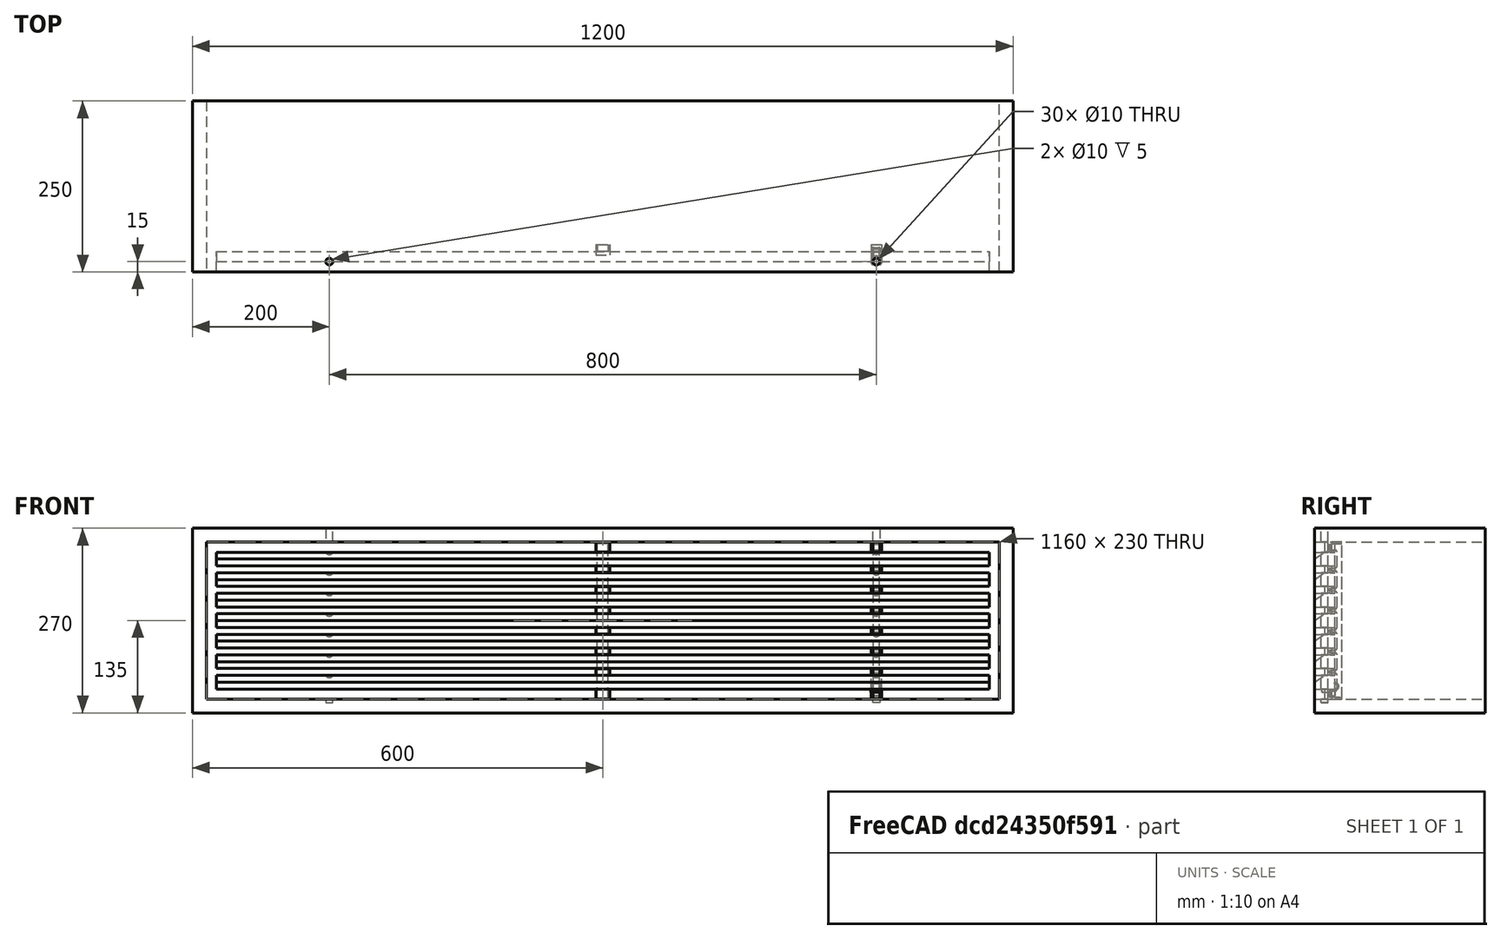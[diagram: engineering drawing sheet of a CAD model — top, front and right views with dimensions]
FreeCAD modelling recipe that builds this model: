
FCSTD DOCUMENT  (FreeCAD 1.0R39109 (Git))
Label: tv cabinet order
License: All rights reserved
objects: TechDraw::DrawViewDimension×24, Sketcher::SketchObject×12, PartDesign::Pad×8, PartDesign::Pocket×7, TechDraw::DrawProjGroupItem×7, PartDesign::Body×6, PartDesign::SubShapeBinder×5, PartDesign::LinearPattern×4, PartDesign::Mirrored×3, PartDesign::Thickness×2, TechDraw::DrawSVGTemplate×2, TechDraw::DrawProjGroup×2, TechDraw::DrawPage×2, TechDraw::DrawViewSection×1, App::DocumentObjectGroup×1, App::VarSet×1
note: 136 computed .brp shape members not serialized (recipe doc carries the construction recipe); baked Part::Feature solids carry a one-line shape summary decoded from their .brp

FEATURE [Sketcher::SketchObject] Sketch
  ArcFitTolerance = 1e-06
  AttachmentSupport = -> [XY_Plane]
  FullyConstrained = true
  MakeInternals = false
  MapMode = 5
  sketch-geometry (5):
    g0: LineSegment StartX=-600 StartY=250 StartZ=0 EndX=-600 EndY=0 EndZ=0
    g1: LineSegment StartX=-600 StartY=0 StartZ=0 EndX=600 EndY=0 EndZ=0
    g2: LineSegment StartX=600 StartY=0 StartZ=0 EndX=600 EndY=250 EndZ=0
    g3: LineSegment StartX=600 StartY=250 StartZ=0 EndX=-600 EndY=250 EndZ=0
    g4: GeomPoint [constr] X=0 Y=125 Z=0
  constraints (13):
    c: Coincident(g0,g1)
    c: Coincident(g1,g2)
    c: Coincident(g2,g3)
    c: Coincident(g3,g0)
    c: Vertical(g0)
    c: Vertical(g2)
    c: Horizontal(g1)
    c: Horizontal(g3)
    c: Symmetric(g2,g0,g4)
    c: PointOnObject(g4,g-2)
    c: DistanceX(g1,g1) = 1200
    c: DistanceY(g2,g2) = 250
    c: PointOnObject(g-1,g1)
FEATURE [PartDesign::Pad] Pad
  Direction = (0,0,1)
  Length = 270
  Length2 = 10
  Profile = -> Sketch
  ReferenceAxis = -> Sketch [N_Axis]
  Suppressed = false
  Type = 0
FEATURE [PartDesign::Thickness] Thickness
  Base = -> Pad [Face2,Face4]
  BaseFeature = -> Pad
  Intersection = false
  Join = 0
  Mode = 0
  Reversed = true
  SupportTransform = false
  Suppressed = false
  Value = 20
FEATURE [Sketcher::SketchObject] Sketch001
  ArcFitTolerance = 1e-06
  AttachmentSupport = -> [XZ_Plane001]
  FullyConstrained = true
  MakeInternals = false
  MapMode = 5
  Placement = pos=(0,0,0) rot=(1,0,0;1.5708rad)
  sketch-geometry (5):
    g0: LineSegment StartX=-565 StartY=55 StartZ=0 EndX=-565 EndY=35 EndZ=0
    g1: LineSegment StartX=-565 StartY=35 StartZ=0 EndX=565 EndY=35 EndZ=0
    g2: LineSegment StartX=565 StartY=35 StartZ=0 EndX=565 EndY=55 EndZ=0
    g3: LineSegment StartX=565 StartY=55 StartZ=0 EndX=-565 EndY=55 EndZ=0
    g4: GeomPoint [constr] X=1e-16 Y=45 Z=0
  constraints (13):
    c: Coincident(g0,g1)
    c: Coincident(g1,g2)
    c: Coincident(g2,g3)
    c: Coincident(g3,g0)
    c: Vertical(g0)
    c: Vertical(g2)
    c: Horizontal(g1)
    c: Horizontal(g3)
    c: Symmetric(g2,g0,g4)
    c: PointOnObject(g4,g-2)
    c: Distance(g2,g2) = 20
    c: Distance(g-1,g1) = 35
    c: DistanceX(g1,g1) = 1130
FEATURE [PartDesign::Pad] Pad001
  Direction = (0,-1,2e-16)
  Length = 30
  Length2 = 10
  Placement = pos=(0,0,0) rot=(1,0,0;1.5708rad)
  Profile = -> Sketch001
  ReferenceAxis = -> Sketch001 [N_Axis]
  Reversed = true
  Suppressed = false
  Type = 0
FEATURE [PartDesign::LinearPattern] LinearPattern
  BaseFeature = -> Pad001
  Direction = -> Z_Axis001
  Length = 180
  Mode = 1
  Occurrences = 7
  Offset = 30
  Placement = pos=(0,0,0) rot=(1,0,0;1.5708rad)
  Suppressed = false
  TransformMode = 1
FEATURE [TechDraw::DrawSVGTemplate] Template
  Height = 210
  Orientation = 1
  Template = /Applications/FreeCAD.app/Contents/Resources/share/Mod/TechDraw/Templates/A4_Landscape_TD.svg
  Width = 297
FEATURE [Sketcher::SketchObject] Sketch002
  ArcFitTolerance = 1e-06
  AttachmentSupport = -> [Thickness]
  FullyConstrained = true
  MakeInternals = false
  MapMode = 5
  Placement = pos=(0,0,270) rot=(0,0,1;0rad)
  sketch-geometry (1):
    g0: Circle CenterX=400 CenterY=15 CenterZ=0 NormalX=0 NormalY=0 NormalZ=1 AngleXU=0 Radius=5
  constraints (3):
    c: Diameter(g0) = 10
    c: DistanceX(g-1,g0) = 400
    c: DistanceY(g-1,g0) = 15
FEATURE [PartDesign::Pocket] Pocket
  BaseFeature = -> Thickness
  Direction = (0,0,-1)
  Length = 0
  Length2 = 5
  Offset = -15
  Profile = -> Sketch002
  ReferenceAxis = -> Sketch002 [N_Axis]
  Suppressed = false
  Type = 3
  UpToFace = -> Thickness [Face2]
FEATURE [PartDesign::Mirrored] Mirrored
  BaseFeature = -> Pocket
  MirrorPlane = -> Sketch002 [V_Axis]
  Originals = -> [Pocket]
  Suppressed = false
  TransformMode = 0
FEATURE [PartDesign::Body] Body
  AllowCompound = true
  Group = -> [Sketch,Pad,Thickness,Sketch002,Pocket,Mirrored]
  Origin = -> Origin
  Tip = -> Mirrored
FEATURE [TechDraw::DrawProjGroupItem] View
  Caption = 前
  CoarseView = false
  Direction = (0,-1,0)
  Focus = 100
  HardHidden = false
  IsoCount = 0
  IsoHidden = false
  IsoVisible = false
  LockPosition = true
  Perspective = false
  Rotation = 0
  RotationVector = (1,0,0)
  Scale = 0.1
  ScaleType = 2
  ScrubCount = 1
  SeamHidden = false
  SeamVisible = false
  SmoothHidden = false
  SmoothVisible = true
  Source = -> [Body]
  Type = 0
  X = 0
  XDirection = (1,0,0)
  Y = 0
FEATURE [TechDraw::DrawProjGroupItem] ProjItem001
  Caption = 下
  CoarseView = false
  Direction = (0,0,-1)
  Focus = 100
  HardHidden = false
  IsoCount = 0
  IsoHidden = false
  IsoVisible = false
  LockPosition = false
  Perspective = false
  Rotation = 0
  RotationVector = (1,0,0)
  Scale = 0.1
  ScaleType = 2
  ScrubCount = 1
  SeamHidden = false
  SeamVisible = false
  SmoothHidden = false
  SmoothVisible = true
  Source = -> [Body]
  Type = 5
  X = 0
  XDirection = (1,0,0)
  Y = -41
FEATURE [TechDraw::DrawProjGroupItem] ProjItem002
  Caption = 右
  CoarseView = false
  Direction = (1,-1e-16,0)
  Focus = 100
  HardHidden = false
  IsoCount = 0
  IsoHidden = false
  IsoVisible = false
  LockPosition = false
  Perspective = false
  Rotation = 0
  RotationVector = (1,0,0)
  Scale = 0.1
  ScaleType = 2
  ScrubCount = 1
  SeamHidden = false
  SeamVisible = false
  SmoothHidden = false
  SmoothVisible = true
  Source = -> [Body]
  Type = 2
  X = 87.5
  XDirection = (1e-16,1,0)
  Y = 0
FEATURE [TechDraw::DrawProjGroupItem] ProjItem
  Caption = 上
  CoarseView = false
  Direction = (0,0,1)
  Focus = 100
  HardHidden = false
  IsoCount = 0
  IsoHidden = false
  IsoVisible = false
  LockPosition = false
  Perspective = false
  Rotation = 0
  RotationVector = (1,0,0)
  Scale = 0.1
  ScaleType = 2
  ScrubCount = 1
  SeamHidden = false
  SeamVisible = false
  SmoothHidden = false
  SmoothVisible = true
  Source = -> [Body]
  Type = 4
  X = 0
  XDirection = (1,0,0)
  Y = 41
FEATURE [TechDraw::DrawProjGroup] ProjGroup
  Anchor = -> View
  AutoDistribute = true
  LockPosition = false
  ProjectionType = 1
  Rotation = 0
  Scale = 0.1
  ScaleType = 2
  Source = -> [Body]
  Views = -> [View,ProjItem001,ProjItem002,ProjItem]
  X = 81.3067
  Y = 133.557
  spacingX = 15
  spacingY = 15
FEATURE [TechDraw::DrawViewDimension] Dimension
  AngleOverride = false
  Arbitrary = false
  ArbitraryTolerances = false
  BoxCorners = (2) [(-60,-13.5,0),(60,13.5,0)]
  EqualTolerance = true
  ExtensionAngle = 0
  FormatSpec = %.2w
  FormatSpecOverTolerance = %+.2w
  FormatSpecUnderTolerance = %+.2w
  Inverted = false
  LineAngle = 0
  LockPosition = false
  MeasureType = 1
  OverTolerance = 0
  References2D = -> [View]
  Rotation = 0
  ScaleType = 0
  TheoreticalExact = false
  Type = 1
  UnderTolerance = 0
  X = 4.02177
  Y = -6.19776
FEATURE [TechDraw::DrawViewDimension] Dimension001
  AngleOverride = false
  Arbitrary = false
  ArbitraryTolerances = false
  BoxCorners = (2) [(-60,-13.5,0),(60,13.5,0)]
  EqualTolerance = true
  ExtensionAngle = 0
  FormatSpec = %.2w
  FormatSpecOverTolerance = %+.2w
  FormatSpecUnderTolerance = %+.2w
  Inverted = false
  LineAngle = 0
  LockPosition = false
  MeasureType = 1
  OverTolerance = 0
  References2D = -> [View]
  Rotation = 0
  ScaleType = 0
  TheoreticalExact = false
  Type = 2
  UnderTolerance = 0
  X = 49.5219
  Y = 0
FEATURE [TechDraw::DrawViewDimension] Dimension002
  AngleOverride = false
  Arbitrary = false
  ArbitraryTolerances = false
  BoxCorners = (2) [(-12.5,-13.5,0),(12.5,13.5,0)]
  EqualTolerance = true
  ExtensionAngle = 0
  FormatSpec = %.2w
  FormatSpecOverTolerance = %+.2w
  FormatSpecUnderTolerance = %+.2w
  Inverted = false
  LineAngle = 0
  LockPosition = false
  MeasureType = 1
  OverTolerance = 0
  References2D = -> [ProjItem002]
  Rotation = 0
  ScaleType = 0
  TheoreticalExact = false
  Type = 1
  UnderTolerance = 0
  X = 0
  Y = -8.38368
FEATURE [TechDraw::DrawViewDimension] Dimension003
  AngleOverride = false
  Arbitrary = false
  ArbitraryTolerances = false
  BoxCorners = (2) [(-60,-12.5,0),(60,12.5,0)]
  EqualTolerance = true
  ExtensionAngle = 0
  FormatSpec = %.2w
  FormatSpecOverTolerance = %+.2w
  FormatSpecUnderTolerance = %+.2w
  Inverted = false
  LineAngle = 0
  LockPosition = false
  MeasureType = 1
  OverTolerance = 0
  References2D = -> [ProjItem]
  Rotation = 0
  ScaleType = 0
  TheoreticalExact = false
  Type = 0
  UnderTolerance = 0
  X = -46.9988
  Y = -6.85586
FEATURE [TechDraw::DrawViewDimension] Dimension004
  AngleOverride = false
  Arbitrary = false
  ArbitraryTolerances = false
  BoxCorners = (2) [(-60,-12.5,0),(60,12.5,0)]
  EqualTolerance = true
  ExtensionAngle = 0
  FormatSpec = %.2w
  FormatSpecOverTolerance = %+.2w
  FormatSpecUnderTolerance = %+.2w
  Inverted = false
  LineAngle = 0
  LockPosition = false
  MeasureType = 1
  OverTolerance = 0
  References2D = -> [ProjItem]
  Rotation = 0
  ScaleType = 0
  TheoreticalExact = false
  Type = 0
  UnderTolerance = 0
  X = -30.5049
  Y = -7.0879
FEATURE [TechDraw::DrawViewDimension] Dimension005
  AngleOverride = false
  Arbitrary = false
  ArbitraryTolerances = false
  BoxCorners = (2) [(-60,-12.5,0),(60,12.5,0)]
  EqualTolerance = true
  ExtensionAngle = 0
  FormatSpec = ⌀%.2w 通孔
  FormatSpecOverTolerance = %+.2w
  FormatSpecUnderTolerance = %+.2w
  Inverted = false
  LineAngle = 0
  LockPosition = false
  MeasureType = 1
  OverTolerance = 0
  References2D = -> [ProjItem]
  Rotation = 0
  ScaleType = 0
  TheoreticalExact = false
  Type = 5
  UnderTolerance = 0
  X = -29.1444
  Y = 3.68719
FEATURE [TechDraw::DrawViewDimension] Dimension006
  AngleOverride = false
  Arbitrary = false
  ArbitraryTolerances = false
  BoxCorners = (2) [(-60,-12.5,0),(60,12.5,0)]
  EqualTolerance = true
  ExtensionAngle = 0
  FormatSpec = %.2w
  FormatSpecOverTolerance = %+.2w
  FormatSpecUnderTolerance = %+.2w
  Inverted = false
  LineAngle = 0
  LockPosition = false
  MeasureType = 1
  OverTolerance = 0
  References2D = -> [ProjItem]
  Rotation = 0
  ScaleType = 0
  TheoreticalExact = false
  Type = 0
  UnderTolerance = 0
  X = 50
  Y = -5.2004
FEATURE [TechDraw::DrawViewDimension] Dimension007
  AngleOverride = false
  Arbitrary = false
  ArbitraryTolerances = false
  BoxCorners = (2) [(-60,-12.5,0),(60,12.5,0)]
  EqualTolerance = true
  ExtensionAngle = 0
  FormatSpec = %.2w
  FormatSpecOverTolerance = %+.2w
  FormatSpecUnderTolerance = %+.2w
  Inverted = false
  LineAngle = 0
  LockPosition = false
  MeasureType = 1
  OverTolerance = 0
  References2D = -> [ProjItem]
  Rotation = 0
  ScaleType = 0
  TheoreticalExact = false
  Type = 0
  UnderTolerance = 0
  X = 30.1157
  Y = -7.33917
FEATURE [TechDraw::DrawViewDimension] Dimension008
  AngleOverride = false
  Arbitrary = false
  ArbitraryTolerances = false
  BoxCorners = (2) [(-60,-12.5,0),(60,12.5,0)]
  EqualTolerance = true
  ExtensionAngle = 0
  FormatSpec = ⌀%.2w 通孔
  FormatSpecOverTolerance = %+.2w
  FormatSpecUnderTolerance = %+.2w
  Inverted = false
  LineAngle = 0
  LockPosition = false
  MeasureType = 1
  OverTolerance = 0
  References2D = -> [ProjItem]
  Rotation = 0
  ScaleType = 0
  TheoreticalExact = false
  Type = 5
  UnderTolerance = 0
  X = 31.0832
  Y = 2.78988
FEATURE [TechDraw::DrawSVGTemplate] Template001
  Height = 210
  Orientation = 1
  Template = /Applications/FreeCAD.app/Contents/Resources/share/Mod/TechDraw/Templates/A4_Landscape_TD.svg
  Width = 297
FEATURE [Sketcher::SketchObject] Sketch003
  ArcFitTolerance = 1e-06
  AttachmentSupport = -> [XY_Plane001]
  FullyConstrained = true
  MakeInternals = false
  MapMode = 5
FEATURE [PartDesign::SubShapeBinder] Binder
  BindCopyOnChange = 0
  BindMode = 0
  ClaimChildren = false
  Context = -> Body001 [Binder.]
  Fuse = false
  MakeFace = true
  OffsetFill = false
  OffsetIntersection = false
  OffsetJoinType = 0
  OffsetOpenResult = false
  PartialLoad = false
  Relative = true
  Support = -> [Body[Sketch002.]]
  _Version = 2
FEATURE [PartDesign::Pocket] Pocket001
  BaseFeature = -> LinearPattern
  Direction = (0,0,-1)
  Length = 5
  Length2 = 5
  Placement = pos=(0,0,0) rot=(1,0,0;1.5708rad)
  Profile = -> Binder
  Suppressed = false
  Type = 1
FEATURE [PartDesign::Mirrored] Mirrored001
  BaseFeature = -> Pocket001
  MirrorPlane = -> YZ_Plane001
  Originals = -> [Pocket001]
  Placement = pos=(0,0,0) rot=(1,0,0;1.5708rad)
  Suppressed = false
  TransformMode = 0
FEATURE [PartDesign::Body] Body001
  AllowCompound = true
  Group = -> [Sketch001,Pad001,LinearPattern,Sketch003,Binder,Pocket001,Mirrored001]
  Origin = -> Origin001
  Tip = -> Mirrored001
FEATURE [TechDraw::DrawProjGroupItem] View001
  Caption = 前
  CoarseView = false
  Direction = (0,-1,0)
  Focus = 100
  HardHidden = false
  IsoCount = 0
  IsoHidden = false
  IsoVisible = false
  LockPosition = true
  Perspective = false
  Rotation = 0
  RotationVector = (1,0,0)
  Scale = 0.2
  ScaleType = 2
  ScrubCount = 1
  SeamHidden = false
  SeamVisible = false
  SmoothHidden = false
  SmoothVisible = true
  Source = -> [Body001]
  Type = 0
  X = 0
  XDirection = (1,0,0)
  Y = 0
FEATURE [TechDraw::DrawProjGroupItem] ProjItem004
  Caption = 右
  CoarseView = false
  Direction = (1,-1e-16,0)
  Focus = 100
  HardHidden = false
  IsoCount = 0
  IsoHidden = false
  IsoVisible = false
  LockPosition = false
  Perspective = false
  Rotation = 0
  RotationVector = (1,0,0)
  Scale = 0.2
  ScaleType = 2
  ScrubCount = 1
  SeamHidden = false
  SeamVisible = false
  SmoothHidden = false
  SmoothVisible = true
  Source = -> [Body001]
  Type = 2
  X = 131
  XDirection = (1e-16,1,0)
  Y = 0
FEATURE [TechDraw::DrawViewDimension] Dimension011
  AngleOverride = false
  Arbitrary = false
  ArbitraryTolerances = false
  BoxCorners = (2) [(-113,-20,0),(113,20,0)]
  EqualTolerance = true
  ExtensionAngle = 0
  FormatSpec = %.2w
  FormatSpecOverTolerance = %+.2w
  FormatSpecUnderTolerance = %+.2w
  Inverted = false
  LineAngle = 0
  LockPosition = false
  MeasureType = 1
  OverTolerance = 0
  References2D = -> [View001]
  Rotation = 0
  ScaleType = 0
  TheoreticalExact = false
  Type = 1
  UnderTolerance = 0
  X = 33.8145
  Y = -37.4036
FEATURE [TechDraw::DrawViewDimension] Dimension012
  AngleOverride = false
  Arbitrary = false
  ArbitraryTolerances = false
  BoxCorners = (2) [(-113,-20,0),(113,20,0)]
  EqualTolerance = true
  ExtensionAngle = 0
  FormatSpec = %.2w
  FormatSpecOverTolerance = %+.2w
  FormatSpecUnderTolerance = %+.2w
  Inverted = false
  LineAngle = 0
  LockPosition = false
  MeasureType = 1
  OverTolerance = 0
  References2D = -> [View001]
  Rotation = 0
  ScaleType = 0
  TheoreticalExact = false
  Type = 0
  UnderTolerance = 0
  X = 118.166
  Y = -36.7115
FEATURE [TechDraw::DrawViewDimension] Dimension013
  AngleOverride = false
  Arbitrary = false
  ArbitraryTolerances = false
  BoxCorners = (2) [(-3,-20,0),(3,20,0)]
  EqualTolerance = true
  ExtensionAngle = 0
  FormatSpec = %.2w
  FormatSpecOverTolerance = %+.2w
  FormatSpecUnderTolerance = %+.2w
  Inverted = false
  LineAngle = 0
  LockPosition = false
  MeasureType = 1
  OverTolerance = 0
  References2D = -> [ProjItem004]
  Rotation = 0
  ScaleType = 0
  TheoreticalExact = false
  Type = 1
  UnderTolerance = 0
  X = 10.4758
  Y = -37.6639
FEATURE [TechDraw::DrawProjGroupItem] ProjItem005
  Caption = 上
  CoarseView = false
  Direction = (0,0,1)
  Focus = 100
  HardHidden = false
  IsoCount = 0
  IsoHidden = false
  IsoVisible = false
  LockPosition = false
  Perspective = false
  Rotation = 0
  RotationVector = (1,0,0)
  ScaleType = 0
  ScrubCount = 1
  SeamHidden = false
  SeamVisible = false
  SmoothHidden = false
  SmoothVisible = true
  Source = -> [Body001]
  Type = 4
  X = 0
  XDirection = (1,0,0)
  Y = 38
FEATURE [TechDraw::DrawProjGroup] ProjGroup001
  Anchor = -> View001
  AutoDistribute = true
  LockPosition = false
  ProjectionType = 1
  Rotation = 0
  Scale = 0.2
  ScaleType = 2
  Source = -> [Body001]
  Views = -> [View001,ProjItem004,ProjItem005]
  X = 129.985
  Y = 125.15
  spacingX = 15
  spacingY = 15
FEATURE [TechDraw::DrawViewDimension] Dimension014
  AngleOverride = false
  Arbitrary = false
  ArbitraryTolerances = false
  BoxCorners = (2) [(-113,-3,0),(113,3,0)]
  EqualTolerance = true
  ExtensionAngle = 0
  FormatSpec = ⌀%.2w 通孔
  FormatSpecOverTolerance = %+.2w
  FormatSpecUnderTolerance = %+.2w
  Inverted = false
  LineAngle = 0
  LockPosition = false
  MeasureType = 1
  OverTolerance = 0
  References2D = -> [ProjItem005]
  Rotation = 0
  ScaleType = 0
  TheoreticalExact = false
  Type = 5
  UnderTolerance = 0
  X = 68.4858
  Y = 10.6024
FEATURE [TechDraw::DrawViewDimension] Dimension015
  AngleOverride = false
  Arbitrary = false
  ArbitraryTolerances = false
  BoxCorners = (2) [(-113,-3,0),(113,3,0)]
  EqualTolerance = true
  ExtensionAngle = 0
  FormatSpec = ⌀%.2w 通孔
  FormatSpecOverTolerance = %+.2w
  FormatSpecUnderTolerance = %+.2w
  Inverted = false
  LineAngle = 0
  LockPosition = false
  MeasureType = 1
  OverTolerance = 0
  References2D = -> [ProjItem005]
  Rotation = 0
  ScaleType = 0
  TheoreticalExact = false
  Type = 5
  UnderTolerance = 0
  X = -73.5147
  Y = 9.63595
FEATURE [TechDraw::DrawViewDimension] Dimension016
  AngleOverride = false
  Arbitrary = false
  ArbitraryTolerances = false
  BoxCorners = (2) [(-113,-3,0),(113,3,0)]
  EqualTolerance = true
  ExtensionAngle = 0
  FormatSpec = %.2w
  FormatSpecOverTolerance = %+.2w
  FormatSpecUnderTolerance = %+.2w
  Inverted = false
  LineAngle = 0
  LockPosition = false
  MeasureType = 1
  OverTolerance = 0
  References2D = -> [ProjItem005]
  Rotation = 0
  ScaleType = 0
  TheoreticalExact = false
  Type = 0
  UnderTolerance = 0
  X = -75.3336
  Y = -8.92378
FEATURE [TechDraw::DrawViewDimension] Dimension017
  AngleOverride = false
  Arbitrary = false
  ArbitraryTolerances = false
  BoxCorners = (2) [(-113,-3,0),(113,3,0)]
  EqualTolerance = true
  ExtensionAngle = 0
  FormatSpec = %.2w
  FormatSpecOverTolerance = %+.2w
  FormatSpecUnderTolerance = %+.2w
  Inverted = false
  LineAngle = 0
  LockPosition = false
  MeasureType = 1
  OverTolerance = 0
  References2D = -> [ProjItem005]
  Rotation = 0
  ScaleType = 0
  TheoreticalExact = false
  Type = 0
  UnderTolerance = 0
  X = -96.5
  Y = -8.92378
FEATURE [TechDraw::DrawViewDimension] Dimension018
  AngleOverride = false
  Arbitrary = false
  ArbitraryTolerances = false
  BoxCorners = (2) [(-113,-3,0),(113,3,0)]
  EqualTolerance = true
  ExtensionAngle = 0
  FormatSpec = %.2w
  FormatSpecOverTolerance = %+.2w
  FormatSpecUnderTolerance = %+.2w
  Inverted = false
  LineAngle = 0
  LockPosition = false
  MeasureType = 1
  OverTolerance = 0
  References2D = -> [ProjItem005]
  Rotation = 0
  ScaleType = 0
  TheoreticalExact = false
  Type = 0
  UnderTolerance = 0
  X = 72.1183
  Y = -9.39892
FEATURE [TechDraw::DrawViewDimension] Dimension019
  AngleOverride = false
  Arbitrary = false
  ArbitraryTolerances = false
  BoxCorners = (2) [(-113,-3,0),(113,3,0)]
  EqualTolerance = true
  ExtensionAngle = 0
  FormatSpec = %.2w
  FormatSpecOverTolerance = %+.2w
  FormatSpecUnderTolerance = %+.2w
  Inverted = false
  LineAngle = 0
  LockPosition = false
  MeasureType = 1
  OverTolerance = 0
  References2D = -> [ProjItem005]
  Rotation = 0
  ScaleType = 0
  TheoreticalExact = false
  Type = 0
  UnderTolerance = 0
  X = 96.5
  Y = -8.92378
FEATURE [TechDraw::DrawPage] Page001
  KeepUpdated = true
  NextBalloonIndex = 1
  ProjectionType = 0
  Template = -> Template001
  Views = -> [ProjGroup001,Dimension011,Dimension012,Dimension013,Dimension014,Dimension015,Dimension016,Dimension017,Dimension018,Dimension019]
FEATURE [TechDraw::DrawViewSection] SectionView001
  BaseView = -> View
  Caption = 底板孔位
  CoarseView = false
  CutSurfaceDisplay = 2
  Direction = (1e-16,0,1)
  FileGeomPattern = /Applications/FreeCAD.app/Contents/Resources/share/Mod/TechDraw/PAT/FCPAT.pat
  FileHatchPattern = /Applications/FreeCAD.app/Contents/Resources/share/Mod/TechDraw/Patterns/simple.svg
  Focus = 100
  FuseBeforeCut = false
  HardHidden = false
  HatchOffset = (0,0,0)
  HatchRotation = 0
  HatchScale = 1
  IsoCount = 0
  IsoHidden = false
  IsoVisible = false
  LockPosition = false
  NameGeomPattern = Diamond
  Perspective = false
  Rotation = 0
  Scale = 0.1
  ScaleType = 2
  ScrubCount = 1
  SeamHidden = false
  SeamVisible = false
  SectionDirection = 4
  SectionLineStretch = 1
  SectionNormal = (1e-16,0,1)
  SectionOrigin = (0,0,21)
  SmoothHidden = false
  SmoothVisible = true
  Source = -> [Body]
  TrimAfterCut = false
  UsePreviousCut = false
  X = 216.148
  XDirection = (1,0,-1e-16)
  Y = 86.6538
FEATURE [TechDraw::DrawViewDimension] Dimension020
  AngleOverride = false
  Arbitrary = false
  ArbitraryTolerances = false
  BoxCorners = (2) [(-60,-12.5,0),(60,12.5,0)]
  EqualTolerance = true
  ExtensionAngle = 0
  FormatSpec = ⌀%.2w 盲孔深5
  FormatSpecOverTolerance = %+.2w
  FormatSpecUnderTolerance = %+.2w
  Inverted = false
  LineAngle = 0
  LockPosition = false
  MeasureType = 1
  OverTolerance = 0
  References2D = -> [SectionView001]
  Rotation = 0
  ScaleType = 0
  TheoreticalExact = false
  Type = 5
  UnderTolerance = 0
  X = -32.7434
  Y = -3.67128
FEATURE [TechDraw::DrawViewDimension] Dimension021
  AngleOverride = false
  Arbitrary = false
  ArbitraryTolerances = false
  BoxCorners = (2) [(-60,-12.5,0),(60,12.5,0)]
  EqualTolerance = true
  ExtensionAngle = 0
  FormatSpec = %.2w
  FormatSpecOverTolerance = %+.2w
  FormatSpecUnderTolerance = %+.2w
  Inverted = false
  LineAngle = 0
  LockPosition = false
  MeasureType = 1
  OverTolerance = 0
  References2D = -> [SectionView001]
  Rotation = 0
  ScaleType = 0
  TheoreticalExact = false
  Type = 0
  UnderTolerance = 0
  X = -36.3187
  Y = -19.83
FEATURE [TechDraw::DrawViewDimension] Dimension022
  AngleOverride = false
  Arbitrary = false
  ArbitraryTolerances = false
  BoxCorners = (2) [(-60,-12.5,0),(60,12.5,0)]
  EqualTolerance = true
  ExtensionAngle = 0
  FormatSpec = %.2w
  FormatSpecOverTolerance = %+.2w
  FormatSpecUnderTolerance = %+.2w
  Inverted = false
  LineAngle = 0
  LockPosition = false
  MeasureType = 1
  OverTolerance = 0
  References2D = -> [SectionView001]
  Rotation = 0
  ScaleType = 0
  TheoreticalExact = false
  Type = 0
  UnderTolerance = 0
  X = -50
  Y = -17.6867
FEATURE [TechDraw::DrawViewDimension] Dimension023
  AngleOverride = false
  Arbitrary = false
  ArbitraryTolerances = false
  BoxCorners = (2) [(-60,-12.5,0),(60,12.5,0)]
  EqualTolerance = true
  ExtensionAngle = 0
  FormatSpec = ⌀%.2w 盲孔深5
  FormatSpecOverTolerance = %+.2w
  FormatSpecUnderTolerance = %+.2w
  Inverted = false
  LineAngle = 0
  LockPosition = false
  MeasureType = 1
  OverTolerance = 0
  References2D = -> [SectionView001]
  Rotation = 0
  ScaleType = 0
  TheoreticalExact = false
  Type = 5
  UnderTolerance = 0
  X = 31.0563
  Y = -2.3135
FEATURE [TechDraw::DrawViewDimension] Dimension024
  AngleOverride = false
  Arbitrary = false
  ArbitraryTolerances = false
  BoxCorners = (2) [(-60,-12.5,0),(60,12.5,0)]
  EqualTolerance = true
  ExtensionAngle = 0
  FormatSpec = %.2w
  FormatSpecOverTolerance = %+.2w
  FormatSpecUnderTolerance = %+.2w
  Inverted = false
  LineAngle = 0
  LockPosition = false
  MeasureType = 1
  OverTolerance = 0
  References2D = -> [SectionView001]
  Rotation = 0
  ScaleType = 0
  TheoreticalExact = false
  Type = 0
  UnderTolerance = 0
  X = 32.4192
  Y = -19.6004
FEATURE [TechDraw::DrawViewDimension] Dimension025
  AngleOverride = false
  Arbitrary = false
  ArbitraryTolerances = false
  BoxCorners = (2) [(-60,-12.5,0),(60,12.5,0)]
  EqualTolerance = true
  ExtensionAngle = 0
  FormatSpec = %.2w
  FormatSpecOverTolerance = %+.2w
  FormatSpecUnderTolerance = %+.2w
  Inverted = false
  LineAngle = 0
  LockPosition = false
  MeasureType = 1
  OverTolerance = 0
  References2D = -> [SectionView001]
  Rotation = 0
  ScaleType = 0
  TheoreticalExact = false
  Type = 0
  UnderTolerance = 0
  X = 50
  Y = -17.6867
FEATURE [TechDraw::DrawPage] Page
  KeepUpdated = true
  NextBalloonIndex = 1
  ProjectionType = 0
  Template = -> Template
  Views = -> [ProjGroup,Dimension,Dimension001,Dimension002,Dimension003,Dimension004,Dimension005,Dimension006,Dimension007,Dimension008,SectionView001,Dimension020,Dimension021,Dimension022,Dimension023,Dimension024,Dimension025]
FEATURE [App::DocumentObjectGroup] Group  label="Drawings"
  Group = -> [Page,Page001]
FEATURE [Sketcher::SketchObject] Sketch004
  ArcFitTolerance = 1e-06
  AttachmentSupport = -> [YZ_Plane002]
  FullyConstrained = true
  MakeInternals = false
  MapMode = 5
  Placement = pos=(0,0,0) rot=(0.57735,0.57735,0.57735;2.0944rad)
  sketch-geometry (7):
    g0: LineSegment StartX=0 StartY=35 StartZ=0 EndX=30 EndY=35 EndZ=0
    g1: LineSegment StartX=30 StartY=35 StartZ=0 EndX=30 EndY=55 EndZ=0
    g2: LineSegment StartX=30 StartY=55 StartZ=0 EndX=15 EndY=55 EndZ=0
    g3: LineSegment [constr] StartX=15 StartY=55 StartZ=0 EndX=0 EndY=55 EndZ=0
    g4: LineSegment [constr] StartX=0 StartY=55 StartZ=0 EndX=0 EndY=45 EndZ=0
    g5: LineSegment StartX=0 StartY=45 StartZ=0 EndX=0 EndY=35 EndZ=0
    g6: LineSegment StartX=0 StartY=45 StartZ=0 EndX=15 EndY=55 EndZ=0
  constraints (20):
    c: Horizontal(g0)
    c: Coincident(g0,g1)
    c: Vertical(g1)
    c: Coincident(g1,g2)
    c: Coincident(g3,g4)
    c: Coincident(g5,g0)
    c: Vertical(g0,g-1)
    c: Distance(g4,g5) = 20
    c: DistanceY(g-1,g0) = 35
    c: Distance(g0,g0) = 30
    c: Coincident(g2,g3)
    c: Horizontal(g2)
    c: Horizontal(g3)
    c: Coincident(g4,g5)
    c: Vertical(g4)
    c: Vertical(g5)
    c: Coincident(g6,g4)
    c: Coincident(g6,g2)
    c: DistanceY(g5,g5) = 10
    c: DistanceX(g3,g3) = 15
FEATURE [PartDesign::Pad] Pad002
  Direction = (1,0,0)
  Length = 1130
  Length2 = 10
  Midplane = true
  Placement = pos=(0,0,0) rot=(1,1,1;2.0944rad)
  Profile = -> Sketch004
  ReferenceAxis = -> Sketch004 [N_Axis]
  Suppressed = false
  Type = 0
FEATURE [PartDesign::LinearPattern] LinearPattern001
  BaseFeature = -> Pad002
  Direction = -> Z_Axis002
  Length = 180
  Mode = 1
  Occurrences = 7
  Offset = 30
  Placement = pos=(0,0,0) rot=(1,1,1;2.0944rad)
  Suppressed = false
  TransformMode = 1
FEATURE [PartDesign::SubShapeBinder] Binder001
  BindCopyOnChange = 0
  BindMode = 0
  ClaimChildren = false
  Context = -> Body002 [Binder001.]
  Fuse = false
  MakeFace = true
  OffsetFill = false
  OffsetIntersection = false
  OffsetJoinType = 0
  OffsetOpenResult = false
  PartialLoad = false
  Relative = true
  Support = -> [Body[Sketch002.]]
  _Version = 2
FEATURE [PartDesign::Pocket] Pocket002
  BaseFeature = -> LinearPattern001
  Direction = (0,0,-1)
  Length = 5
  Length2 = 5
  Placement = pos=(0,0,0) rot=(1,1,1;2.0944rad)
  Profile = -> Binder001
  Suppressed = false
  Type = 1
FEATURE [PartDesign::Mirrored] Mirrored002
  BaseFeature = -> Pocket002
  MirrorPlane = -> YZ_Plane002
  Originals = -> [Pocket002]
  Placement = pos=(0,0,0) rot=(1,1,1;2.0944rad)
  Suppressed = false
  TransformMode = 0
FEATURE [PartDesign::Body] Body002
  AllowCompound = true
  Group = -> [Sketch004,Pad002,LinearPattern001,Binder001,Pocket002,Mirrored002]
  Origin = -> Origin002
  Tip = -> Mirrored002
FEATURE [Sketcher::SketchObject] Sketch005
  ArcFitTolerance = 1e-06
  AttachmentOffset = pos=(0,0,400) rot=(0,0,1;0rad)
  AttachmentSupport = -> [YZ_Plane003]
  FullyConstrained = true
  MakeInternals = false
  MapMode = 5
  Placement = pos=(400,0,0) rot=(0.57735,0.57735,0.57735;2.0944rad)
  sketch-geometry (4):
    g0: LineSegment StartX=15 StartY=249.9 StartZ=0 EndX=15 EndY=20.1 EndZ=0
    g1: LineSegment StartX=15 StartY=20.1 StartZ=0 EndX=40 EndY=20.1 EndZ=0
    g2: LineSegment StartX=40 StartY=20.1 StartZ=0 EndX=40 EndY=249.9 EndZ=0
    g3: LineSegment StartX=40 StartY=249.9 StartZ=0 EndX=15 EndY=249.9 EndZ=0
  constraints (12):
    c: Coincident(g0,g1)
    c: Coincident(g1,g2)
    c: Coincident(g2,g3)
    c: Coincident(g3,g0)
    c: Vertical(g0)
    c: Vertical(g2)
    c: Horizontal(g1)
    c: Horizontal(g3)
    c: Distance(g-1,g1) = 20.1
    c: DistanceY(g2,g2) = 229.8
    c: Distance(g1,g1) = 25
    c: Distance(g-2,g0) = 15
FEATURE [PartDesign::Pad] Pad003
  Direction = (1,0,0)
  Length = 15
  Length2 = 10
  Midplane = true
  Placement = pos=(0,0,0) rot=(1,1,1;2.0944rad)
  Profile = -> Sketch005
  ReferenceAxis = -> Sketch005 [N_Axis]
  Suppressed = false
  Type = 0
FEATURE [PartDesign::SubShapeBinder] Binder003
  BindCopyOnChange = 0
  BindMode = 0
  ClaimChildren = false
  Context = -> Body003 [Binder003.]
  Fuse = false
  MakeFace = true
  Offset = 0.1
  OffsetFill = false
  OffsetIntersection = false
  OffsetJoinType = 0
  OffsetOpenResult = false
  PartialLoad = false
  Relative = true
  Support = -> [Body[Sketch002.]]
  _Version = 2
FEATURE [PartDesign::Pocket] Pocket003
  BaseFeature = -> Pad003
  Direction = (0,0,-1)
  Length = 5
  Length2 = 5
  Placement = pos=(0,0,0) rot=(1,1,1;2.0944rad)
  Profile = -> Binder003
  Suppressed = false
  Type = 1
FEATURE [Sketcher::SketchObject] Sketch006
  ArcFitTolerance = 1e-06
  AttachmentSupport = -> [YZ_Plane003]
  FullyConstrained = true
  MakeInternals = false
  MapMode = 5
  Placement = pos=(0,0,0) rot=(0.57735,0.57735,0.57735;2.0944rad)
  sketch-geometry (4):
    g0: LineSegment StartX=30 StartY=34.9 StartZ=0 EndX=30 EndY=55.1 EndZ=0
    g1: LineSegment StartX=30 StartY=55.1 StartZ=0 EndX=0 EndY=55.1 EndZ=0
    g2: LineSegment StartX=0 StartY=55.1 StartZ=0 EndX=0 EndY=34.9 EndZ=0
    g3: LineSegment StartX=0 StartY=34.9 StartZ=0 EndX=30 EndY=34.9 EndZ=0
  constraints (12):
    c: Coincident(g0,g1)
    c: Coincident(g1,g2)
    c: Coincident(g2,g3)
    c: Coincident(g3,g0)
    c: Vertical(g0)
    c: Vertical(g2)
    c: Horizontal(g1)
    c: Horizontal(g3)
    c: PointOnObject(g1,g-2)
    c: Distance(g3,g3) = 30
    c: DistanceY(g-1,g2) = 34.9
    c: DistanceY(g0,g0) = 20.2
FEATURE [PartDesign::Pocket] Pocket004
  BaseFeature = -> Pocket003
  Direction = (-1,0,0)
  Length = 5
  Length2 = 5
  Midplane = true
  Placement = pos=(0,0,0) rot=(1,1,1;2.0944rad)
  Profile = -> Sketch006
  ReferenceAxis = -> Sketch006 [N_Axis]
  Suppressed = false
  Type = 1
FEATURE [PartDesign::LinearPattern] LinearPattern002
  BaseFeature = -> Pocket004
  Direction = -> Z_Axis003
  Length = 180
  Mode = 1
  Occurrences = 7
  Offset = 30
  Originals = -> [Pocket004]
  Placement = pos=(0,0,0) rot=(1,1,1;2.0944rad)
  Suppressed = false
  TransformMode = 0
FEATURE [PartDesign::Thickness] Thickness001
  Base = -> LinearPattern002 [Face9]
  BaseFeature = -> LinearPattern002
  Intersection = true
  Join = 0
  Mode = 0
  Reversed = true
  SupportTransform = false
  Suppressed = false
  Value = 3
FEATURE [PartDesign::Body] Body003
  AllowCompound = true
  Group = -> [Sketch005,Pad003,Binder003,Pocket003,Sketch006,Pocket004,LinearPattern002,Thickness001]
  Origin = -> Origin003
  Tip = -> Thickness001
FEATURE [PartDesign::SubShapeBinder] Binder004
  BindCopyOnChange = 0
  BindMode = 0
  ClaimChildren = false
  Context = -> Body004 [Binder004.]
  Fuse = false
  MakeFace = true
  OffsetFill = false
  OffsetIntersection = false
  OffsetJoinType = 0
  OffsetOpenResult = false
  PartialLoad = false
  Relative = true
  Support = -> [Body[Sketch002.]]
  _Version = 2
FEATURE [Sketcher::SketchObject] Sketch007
  ArcFitTolerance = 1e-06
  AttachmentOffset = pos=(0,0,35) rot=(0,0,1;0rad)
  AttachmentSupport = -> [XY_Plane004]
  ExternalGeometry = -> [Binder004]
  FullyConstrained = true
  MakeInternals = false
  MapMode = 5
  Placement = pos=(0,0,35) rot=(0,0,1;0rad)
  sketch-geometry (10):
    g0: ArcOfCircle CenterX=400 CenterY=15 CenterZ=0 NormalX=0 NormalY=0 NormalZ=1 AngleXU=0 Radius=4.9 StartAngle=5.86274 EndAngle=9.84522
    g1: ArcOfCircle CenterX=394.157 CenterY=12.3878 CenterZ=0 NormalX=0 NormalY=0 NormalZ=1 AngleXU=0 Radius=1.5 StartAngle=3.56203 EndAngle=6.70363
    g2: ArcOfCircle CenterX=405.843 CenterY=12.3878 CenterZ=0 NormalX=0 NormalY=0 NormalZ=1 AngleXU=0 Radius=1.5 StartAngle=2.72115 EndAngle=5.86274
    g3: ArcOfCircle CenterX=400 CenterY=15 CenterZ=0 NormalX=0 NormalY=0 NormalZ=1 AngleXU=0 Radius=7.9 StartAngle=2.35614 EndAngle=3.56203
    g4: ArcOfCircle CenterX=400 CenterY=15 CenterZ=0 NormalX=0 NormalY=0 NormalZ=1 AngleXU=0 Radius=7.9 StartAngle=5.86274 EndAngle=7.06863
    g5: ArcOfCircle CenterX=393 CenterY=22.0007 CenterZ=0 NormalX=0 NormalY=0 NormalZ=1 AngleXU=0 Radius=2 StartAngle=5.49774 EndAngle=6.28319
    g6: ArcOfCircle CenterX=407 CenterY=22.0007 CenterZ=0 NormalX=0 NormalY=0 NormalZ=1 AngleXU=0 Radius=2 StartAngle=3.14159 EndAngle=3.92704
    g7: LineSegment StartX=395 StartY=22.0007 StartZ=0 EndX=395 EndY=30 EndZ=0
    g8: LineSegment StartX=405 StartY=22.0007 StartZ=0 EndX=405 EndY=30 EndZ=0
    g9: LineSegment StartX=395 StartY=30 StartZ=0 EndX=405 EndY=30 EndZ=0
  constraints (26):
    c: Coincident(g0,g-3)
    c: Horizontal(g0,g0)
    c: DistanceY(g0,g0) = 2
    c: Tangent(g1,g0) = 1.5708
    c: Tangent(g2,g0) = 1.5708
    c: Horizontal(g2,g1)
    c: Radius(g2) = 1.5
    c: Coincident(g3,g0)
    c: Coincident(g4,g0)
    c: Tangent(g3,g1) = -1.5708
    c: Tangent(g4,g2) = -1.5708
    c: Horizontal(g3,g4)
    c: Vertical(g7)
    c: Vertical(g8)
    c: Tangent(g5,g3) = 1.5708
    c: Tangent(g6,g4) = 1.5708
    c: Tangent(g7,g5) = -1.5708
    c: Tangent(g8,g6) = 1.5708
    c: Horizontal(g5,g6)
    c: Coincident(g9,g7)
    c: Coincident(g9,g8)
    c: Horizontal(g9)
    c: DistanceY(g-1,g8) = 30
    c: Radius(g5) = 2
    c: Distance(g9,g9) = 10
    c: Radius(g0) = 4.9
FEATURE [PartDesign::Pad] Pad004
  Direction = (0,0,1)
  Length = 5
  Length2 = 10
  Profile = -> Sketch007
  ReferenceAxis = -> Sketch007 [N_Axis]
  Reversed = true
  Suppressed = false
  Type = 0
  expr: Length = VarSet.ArmHeight
FEATURE [Sketcher::SketchObject] Sketch008
  ArcFitTolerance = 1e-06
  AttachmentSupport = -> [Pad004]
  ExternalGeometry = -> [Sketch007]
  FullyConstrained = true
  MakeInternals = false
  MapMode = 5
  Placement = pos=(0,0,30) rot=(1,0,0;3.14159rad)
  sketch-geometry (4):
    g0: LineSegment StartX=395 StartY=-22.0007 StartZ=0 EndX=395 EndY=-30 EndZ=0
    g1: LineSegment StartX=395 StartY=-30 StartZ=0 EndX=405 EndY=-30 EndZ=0
    g2: LineSegment StartX=405 StartY=-30 StartZ=0 EndX=405 EndY=-22.0007 EndZ=0
    g3: LineSegment StartX=405 StartY=-22.0007 StartZ=0 EndX=395 EndY=-22.0007 EndZ=0
  constraints (10):
    c: Coincident(g0,g1)
    c: Coincident(g1,g2)
    c: Coincident(g2,g3)
    c: Coincident(g3,g0)
    c: Vertical(g0)
    c: Vertical(g2)
    c: Horizontal(g1)
    c: Horizontal(g3)
    c: Coincident(g0,g-3)
    c: Coincident(g1,g-4)
FEATURE [PartDesign::Pad] Pad005
  BaseFeature = -> Pad004
  Direction = (0,0,-1)
  Length = 5
  Length2 = 10
  Profile = -> Sketch008
  ReferenceAxis = -> Sketch008 [N_Axis]
  Suppressed = false
  Type = 0
  expr: Length = VarSet.Gap - VarSet.ArmHeight
FEATURE [Sketcher::SketchObject] Sketch009
  ArcFitTolerance = 1e-06
  AttachmentSupport = -> [Pad005]
  ExternalGeometry = -> [Sketch007]
  FullyConstrained = true
  MakeInternals = false
  MapMode = 5
  Placement = pos=(405,0,0) rot=(0.57735,0.57735,0.57735;2.0944rad)
  sketch-geometry (5):
    g0: ArcOfCircle CenterX=30 CenterY=38.75 CenterZ=0 NormalX=0 NormalY=0 NormalZ=1 AngleXU=0 Radius=3.75 StartAngle=4.71239 EndAngle=7.85398
    g1: LineSegment StartX=30 StartY=35 StartZ=0 EndX=30 EndY=31.2625 EndZ=0
    g2: ArcOfCircle CenterX=30 CenterY=38.75 CenterZ=0 NormalX=0 NormalY=0 NormalZ=1 AngleXU=0 Radius=5.75 StartAngle=4.97341 EndAngle=7.85398
    g3: ArcOfCircle CenterX=32 CenterY=31.2625 CenterZ=0 NormalX=0 NormalY=0 NormalZ=1 AngleXU=0 Radius=2 StartAngle=1.83181 EndAngle=3.14159
    g4: ArcOfCircle CenterX=30 CenterY=43.5 CenterZ=0 NormalX=0 NormalY=0 NormalZ=1 AngleXU=0 Radius=1 StartAngle=1.5708 EndAngle=4.71239
  constraints (13):
    c: Coincident(g1,g0)
    c: Vertical(g1)
    c: Coincident(g2,g0)
    c: Tangent(g3,g1) = -1.5708
    c: Tangent(g3,g2) = 1.5708
    c: Coincident(g0,g-3)
    c: Tangent(g4,g2) = -1.5708
    c: Tangent(g4,g0) = 1.5708
    c: Vertical(g4,g0)
    c: Vertical(g0,g0)
    c: Radius(g3) = 2
    c: DistanceY(g0,g2) = 9.5
    c: Distance(g0,g2) = 2
FEATURE [PartDesign::Pad] Pad006
  BaseFeature = -> Pad005
  Direction = (1,0,0)
  Length = 10
  Length2 = 10
  Profile = -> Sketch009
  ReferenceAxis = -> Sketch009 [N_Axis]
  Reversed = true
  Suppressed = false
  Type = 3
  UpToFace = -> Pad005 [Face9]
FEATURE [App::VarSet] VarSet
  ArmHeight = 5
  Gap = 10
FEATURE [PartDesign::Body] Body004
  AllowCompound = true
  Group = -> [Binder004,Sketch007,Pad004,Sketch008,Pad005,Sketch009,Pad006,VarSet]
  Origin = -> Origin004
  Tip = -> Pad006
FEATURE [Sketcher::SketchObject] Sketch010
  ArcFitTolerance = 1e-06
  AttachmentSupport = -> [YZ_Plane005]
  FullyConstrained = true
  MakeInternals = false
  MapMode = 5
  Placement = pos=(0,0,0) rot=(0.57735,0.57735,0.57735;2.0944rad)
  sketch-geometry (4):
    g0: LineSegment StartX=25 StartY=250 StartZ=0 EndX=25 EndY=20 EndZ=0
    g1: LineSegment StartX=25 StartY=20 StartZ=0 EndX=40 EndY=20 EndZ=0
    g2: LineSegment StartX=40 StartY=20 StartZ=0 EndX=40 EndY=250 EndZ=0
    g3: LineSegment StartX=40 StartY=250 StartZ=0 EndX=25 EndY=250 EndZ=0
  constraints (12):
    c: Coincident(g0,g1)
    c: Coincident(g1,g2)
    c: Coincident(g2,g3)
    c: Coincident(g3,g0)
    c: Vertical(g0)
    c: Vertical(g2)
    c: Horizontal(g1)
    c: Horizontal(g3)
    c: Distance(g0,g-2) = 25
    c: Distance(g0,g-1) = 20
    c: Distance(g0,g0) = 230
    c: Distance(g1,g-2) = 40
FEATURE [PartDesign::Pad] Pad007
  Direction = (1,0,0)
  Length = 20
  Length2 = 10
  Midplane = true
  Placement = pos=(0,0,0) rot=(1,1,1;2.0944rad)
  Profile = -> Sketch010
  ReferenceAxis = -> Sketch010 [N_Axis]
  Suppressed = false
  Type = 0
FEATURE [Sketcher::SketchObject] Sketch011
  ArcFitTolerance = 1e-06
  AttachmentSupport = -> [YZ_Plane005]
  FullyConstrained = true
  MakeInternals = false
  MapMode = 5
  Placement = pos=(0,0,0) rot=(0.57735,0.57735,0.57735;2.0944rad)
  sketch-geometry (5):
    g0: LineSegment StartX=0 StartY=55.2 StartZ=0 EndX=0 EndY=34.8 EndZ=0
    g1: LineSegment StartX=0 StartY=34.8 StartZ=0 EndX=30 EndY=34.8 EndZ=0
    g2: LineSegment StartX=30 StartY=34.8 StartZ=0 EndX=30 EndY=55.2 EndZ=0
    g3: LineSegment StartX=30 StartY=55.2 StartZ=0 EndX=0 EndY=55.2 EndZ=0
    g4: GeomPoint [constr] X=15 Y=45 Z=0
  constraints (13):
    c: Coincident(g0,g1)
    c: Coincident(g1,g2)
    c: Coincident(g2,g3)
    c: Coincident(g3,g0)
    c: Vertical(g0)
    c: Vertical(g2)
    c: Horizontal(g1)
    c: Horizontal(g3)
    c: Symmetric(g2,g0,g4)
    c: DistanceY(g2,g2) = 20.4
    c: DistanceY(g-1,g4) = 45
    c: PointOnObject(g0,g-2)
    c: DistanceX(g1,g1) = 30
FEATURE [PartDesign::Pocket] Pocket005
  BaseFeature = -> Pad007
  Direction = (-1,0,0)
  Length = 5
  Length2 = 5
  Midplane = true
  Placement = pos=(0,0,0) rot=(1,1,1;2.0944rad)
  Profile = -> Sketch011
  ReferenceAxis = -> Sketch011 [N_Axis]
  Suppressed = false
  Type = 1
FEATURE [PartDesign::LinearPattern] LinearPattern003
  BaseFeature = -> Pocket005
  Direction = -> Z_Axis005
  Length = 180
  Mode = 1
  Occurrences = 7
  Offset = 30
  Originals = -> [Pocket005]
  Placement = pos=(0,0,0) rot=(1,1,1;2.0944rad)
  Suppressed = false
  TransformMode = 0
FEATURE [PartDesign::SubShapeBinder] Binder005
  BindCopyOnChange = 0
  BindMode = 0
  ClaimChildren = false
  Context = -> Body005 [Binder005.]
  Fuse = false
  MakeFace = true
  Offset = -2
  OffsetFill = false
  OffsetIntersection = false
  OffsetJoinType = 0
  OffsetOpenResult = false
  PartialLoad = false
  Relative = true
  Support = -> [LinearPattern003[Face6]]
  _Version = 2
FEATURE [PartDesign::Pocket] Pocket006
  BaseFeature = -> LinearPattern003
  Direction = (7e-16,1,0)
  Length = 10
  Length2 = 5
  Placement = pos=(0,0,0) rot=(1,1,1;2.0944rad)
  Profile = -> Binder005
  Reversed = true
  Suppressed = false
  Type = 0
FEATURE [PartDesign::Body] Body005
  AllowCompound = true
  Group = -> [Sketch010,Pad007,Sketch011,Pocket005,LinearPattern003,Binder005,Pocket006]
  Origin = -> Origin005
  Tip = -> Pocket006
